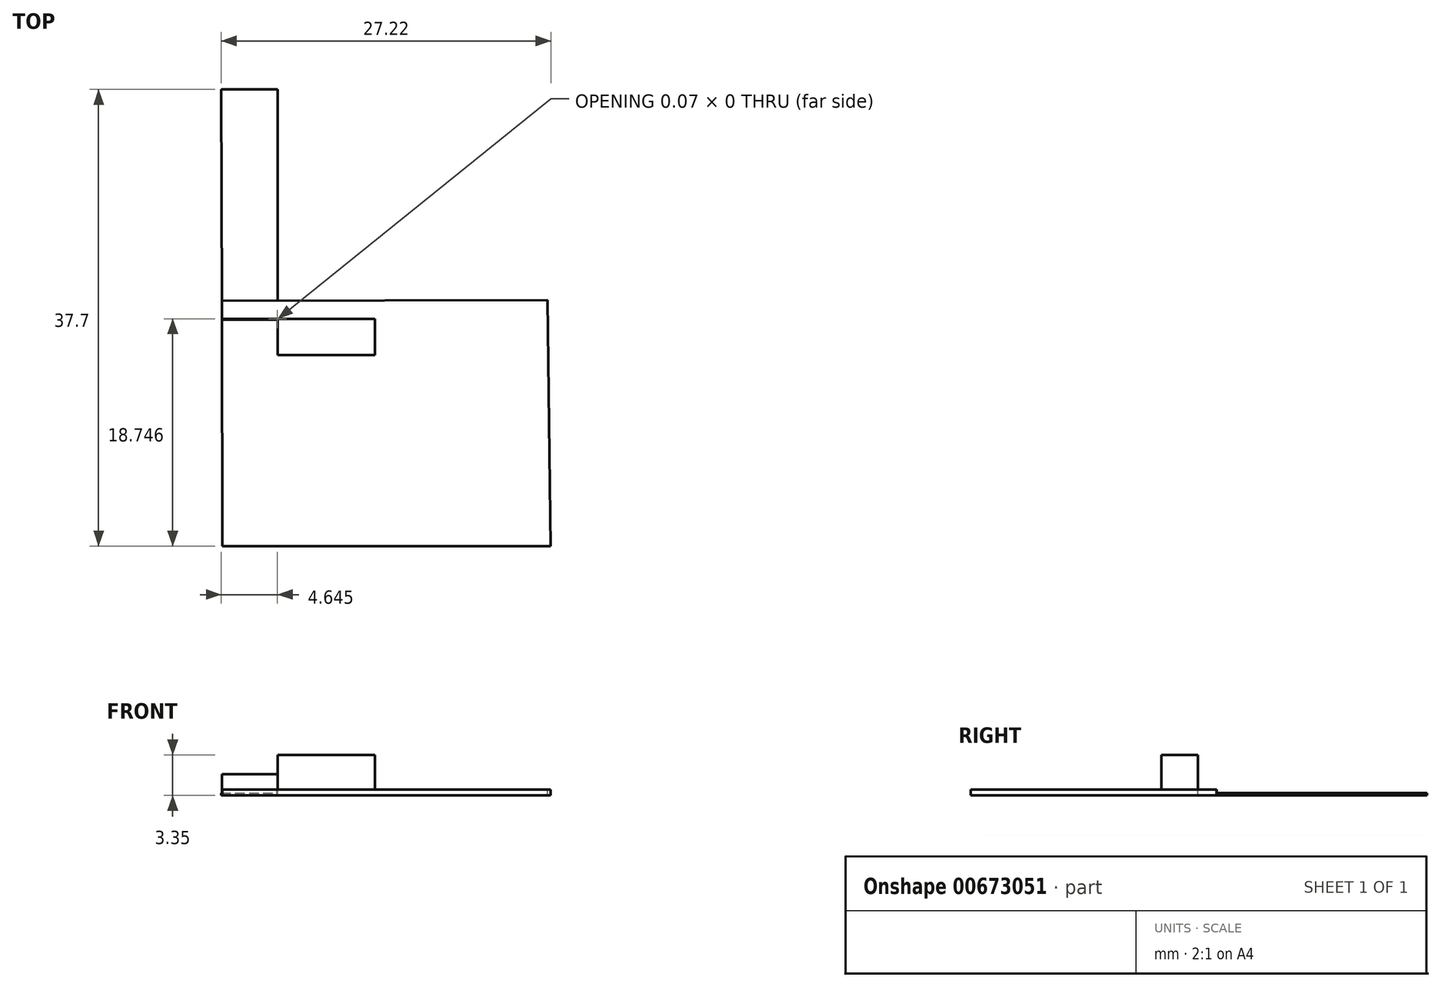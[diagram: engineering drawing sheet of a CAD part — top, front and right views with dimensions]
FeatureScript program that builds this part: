
annotation { "Feature Type Name" : "Feature", "Feature Type Description" : "" }
export const myFeature = defineFeature(function(context is Context, id is Id, definition is map)
    precondition{}
    {
        {
            var Q0;
            Q0=qCreatedBy(makeId("Top.planeOp"),FACE);
            var sketch = newSketch(context, id + "F0", { "sketchPlane" : qUnion([Q0])});
            skLineSegment(sketch, "E0", {"start": v(40.49, 22.18) * mm, "end": v(54.42, 22.18) * mm});
            skLineSegment(sketch, "E1", {"start": v(54.42, 22.18) * mm, "end": v(56.91, 20.67) * mm});
            skLineSegment(sketch, "E2", {"start": v(56.91, 20.67) * mm, "end": v(61.9, 20.67) * mm});
            skLineSegment(sketch, "E3", {"start": v(61.9, 20.67) * mm, "end": v(64.38, 22.18) * mm});
            skLineSegment(sketch, "E4", {"start": v(64.38, 22.18) * mm, "end": v(67.23, 22.18) * mm});
            skLineSegment(sketch, "E5", {"start": v(67.23, 22.18) * mm, "end": v(67.7, -15.52) * mm});
            skLineSegment(sketch, "E6", {"start": v(67.7, -15.52) * mm, "end": v(40.59, -15.52) * mm});
            skLineSegment(sketch, "E7", {"start": v(40.59, -15.52) * mm, "end": v(40.49, 22.18) * mm});
            skLineSegment(sketch, "E8", {"start": v(40.54, 3.23) * mm, "end": v(67.47, 3.23) * mm});
            skLineSegment(sketch, "E9", {"start": v(40.53, 4.73) * mm, "end": v(67.45, 4.8) * mm});
            skPoint(sketch, "E10", {"position": v(70.89, -15.53) * mm});
            skLineSegment(sketch, "E11", {"start": v(51.35, 17.27) * mm, "end": v(59.43, 17.37) * mm});
            skLineSegment(sketch, "E12", {"start": v(59.43, 17.37) * mm, "end": v(59.53, 8.82) * mm});
            skLineSegment(sketch, "E13", {"start": v(59.53, 8.82) * mm, "end": v(51.42, 8.72) * mm});
            skLineSegment(sketch, "E14", {"start": v(51.42, 8.72) * mm, "end": v(51.35, 17.27) * mm});
            skLineSegment(sketch, "E15", {"start": v(55.26, 8.76) * mm, "end": v(54.57, 7.5) * mm});
            skLineSegment(sketch, "E16", {"start": v(54.57, 7.5) * mm, "end": v(52.83, 7.47) * mm});
            skLineSegment(sketch, "E17", {"start": v(52.83, 7.47) * mm, "end": v(52.1, 8.72) * mm});
            skLineSegment(sketch, "E18", {"start": v(45.17, 3.23) * mm, "end": v(45.17, 0.24) * mm});
            skLineSegment(sketch, "E19", {"start": v(45.17, 0.24) * mm, "end": v(59.6, 0.24) * mm});
            skLineSegment(sketch, "E20", {"start": v(59.6, 0.24) * mm, "end": v(59.55, -8.91) * mm});
            skLineSegment(sketch, "E21", {"start": v(59.55, -8.91) * mm, "end": v(51.6, -8.91) * mm});
            skLineSegment(sketch, "E22", {"start": v(51.6, -8.91) * mm, "end": v(51.6, 0.24) * mm});
            skLineSegment(sketch, "E23", {"start": v(53.17, 3.23) * mm, "end": v(53.17, 0.24) * mm});
            skLineSegment(sketch, "E24", {"start": v(45.17, 3.23) * mm, "end": v(45.17, 22.18) * mm});
            skLineSegment(sketch, "E25", {"start": v(45.17, 0.24) * mm, "end": v(45.17, -15.52) * mm});
            skLineSegment(sketch, "E26", {"start": v(40.54, 3.21) * mm, "end": v(45.17, 3.23) * mm});
            skLineSegment(sketch, "E27", {"start": v(40.54, 3.16) * mm, "end": v(45.17, 3.18) * mm});
            skSolve(sketch);
        }
        {
            var Q0;
            {var subQ0=sQuery(id+"F0.wireOp",EDGE,"E8");var subQ1=sQuery(id+"F0.wireOp",EDGE,"E7");var subQ2=makeQuery(id+"F0.imprint","INTERSECT",VERTEX,{"derivedFrom":[subQ1,subQ0]});Q0=makeQuery(id+"F0.imprint","IMPRINT",FACE,{"disambiguationData":[TD([[makeQuery(id+"F0.imprint","IMPRINT",EDGE,{"disambiguationData":[TD([[subQ2,-1.0]])],"derivedFrom":subQ1}),-1.0]])]});}
            var Q1;
            {var subQ1=sQuery(id+"F0.wireOp",EDGE,"E5");var subQ5=sQuery(id+"F0.wireOp",EDGE,"E8");var subQ6=makeQuery(id+"F0.imprint","INTERSECT",VERTEX,{"derivedFrom":[subQ1,subQ5]});Q1=makeQuery(id+"F0.imprint","IMPRINT",FACE,{"disambiguationData":[TD([[makeQuery(id+"F0.imprint","IMPRINT",EDGE,{"disambiguationData":[TD([[subQ6,1.0]])],"derivedFrom":subQ1}),-1.0]])]});}
            var Q2;
            {var subQ0=sQuery(id+"F0.wireOp",EDGE,"E25");Q2=makeQuery(id+"F0.imprint","IMPRINT",FACE,{"disambiguationData":[TD([[makeQuery(id+"F0.imprint","IMPRINT",EDGE,{"derivedFrom":subQ0}),-1.0]])]});}
            var Q3;
            {var subQ7=sQuery(id+"F0.wireOp",EDGE,"E23");Q3=makeQuery(id+"F0.imprint","IMPRINT",FACE,{"disambiguationData":[TD([[makeQuery(id+"F0.imprint","IMPRINT",EDGE,{"derivedFrom":subQ7}),-1.0]])]});}
            var Q4;
            {var subQ9=sQuery(id+"F0.wireOp",EDGE,"E20");Q4=makeQuery(id+"F0.imprint","IMPRINT",FACE,{"disambiguationData":[TD([[makeQuery(id+"F0.imprint","IMPRINT",EDGE,{"derivedFrom":subQ9}),1.0]])]});}
            var Q5;
            {var subQ0=sQuery(id+"F0.wireOp",EDGE,"E20");Q5=makeQuery(id+"F0.imprint","IMPRINT",FACE,{"disambiguationData":[TD([[makeQuery(id+"F0.imprint","IMPRINT",EDGE,{"derivedFrom":subQ0}),-1.0]])]});}
            var Q6;
            {var subQ7=sQuery(id+"F0.wireOp",EDGE,"E27");Q6=makeQuery(id+"F0.imprint","IMPRINT",FACE,{"disambiguationData":[TD([[makeQuery(id+"F0.imprint","IMPRINT",EDGE,{"derivedFrom":subQ7}),1.0]])]});}
            var Q7;
            {var subQ0=sQuery(id+"F0.wireOp",EDGE,"E8");var subQ1=sQuery(id+"F0.wireOp",EDGE,"E7");var subQ2=makeQuery(id+"F0.imprint","INTERSECT",VERTEX,{"derivedFrom":[subQ1,subQ0]});Q7=makeQuery(id+"F0.imprint","IMPRINT",FACE,{"disambiguationData":[TD([[makeQuery(id+"F0.imprint","IMPRINT",EDGE,{"disambiguationData":[TD([[subQ2,1.0]])],"derivedFrom":subQ1}),-1.0]])]});}
            extrude(context, id + "F1", {"entities" : qUnion([Q0, Q1, Q2, Q3, Q4, Q5, Q6, Q7]), "oppositeDirection" : true, "depth" : 0.5 * mm, "offsetDistance" : 25 * mm});
        }
        {
            var Q0;
            {var subQ1=sQuery(id+"F0.wireOp",EDGE,"E18");Q0=makeQuery(id+"F0.imprint","IMPRINT",FACE,{"disambiguationData":[TD([[makeQuery(id+"F0.imprint","IMPRINT",EDGE,{"derivedFrom":subQ1}),1.0]])]});}
            extrude(context, id + "F2", {"entities" : qUnion([Q0]), "depth" : 2.85 * mm, "offsetDistance" : 25 * mm});
        }
        {
            var Q0;
            {var subQ0=sQuery(id+"F0.wireOp",EDGE,"E7");var subQ1=sQuery(id+"F0.wireOp",EDGE,"E0");var subQ2=makeQuery(id+"F0.imprint","INTERSECT",VERTEX,{"derivedFrom":[subQ1,subQ0]});Q0=makeQuery(id+"F0.imprint","IMPRINT",FACE,{"disambiguationData":[TD([[makeQuery(id+"F0.imprint","IMPRINT",EDGE,{"disambiguationData":[TD([[subQ2,-1.0]])],"derivedFrom":subQ1}),-1.0]])]});}
            extrude(context, id + "F3", {"entities" : qUnion([Q0]), "oppositeDirection" : true, "depth" : .5 * mm, "offsetDistance" : 25 * mm, "hasSecondDirection" : true, "secondDirectionOppositeDirection" : true, "secondDirectionDepth" : 0.3 * mm});
        }
        {
            var Q0;
            {var subQ7=sQuery(id+"F0.wireOp",EDGE,"E27");Q0=makeQuery(id+"F0.imprint","IMPRINT",FACE,{"disambiguationData":[TD([[makeQuery(id+"F0.imprint","IMPRINT",EDGE,{"derivedFrom":subQ7}),1.0]])]});}
            extrude(context, id + "F4", {"entities" : qUnion([Q0]), "depth" : 1.25 * mm, "offsetDistance" : 25 * mm});
        }
    });
